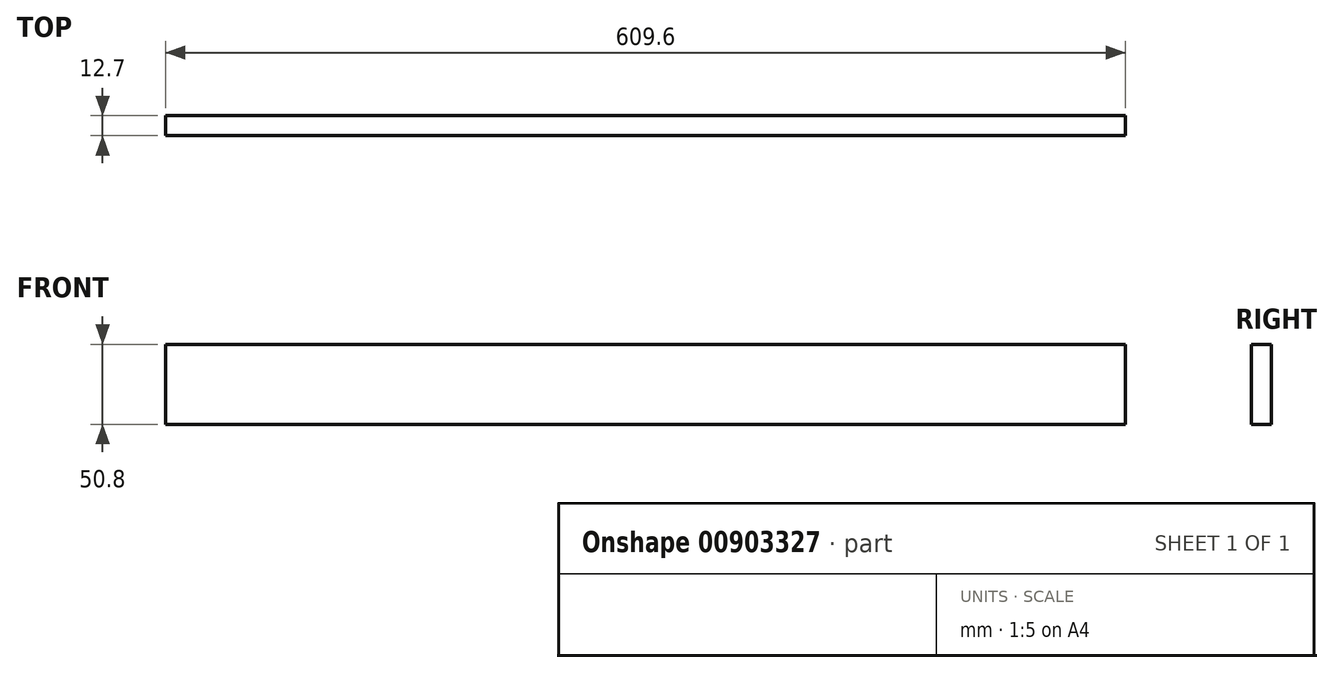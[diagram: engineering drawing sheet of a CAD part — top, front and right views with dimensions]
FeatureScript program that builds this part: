
annotation { "Feature Type Name" : "Feature", "Feature Type Description" : "" }
export const myFeature = defineFeature(function(context is Context, id is Id, definition is map)
    precondition{}
    {
        {
            var Q0;
            Q0=qCreatedBy(makeId("Right.planeOp"),FACE);
            var sketch = newSketch(context, id + "F0", { "sketchPlane" : qUnion([Q0])});
            skLineSegment(sketch, "E0.bottom", {"start": v(-25.21, 17.4) * mm, "end": v(-12.51, 17.4) * mm});
            skLineSegment(sketch, "E0.top", {"start": v(-25.21, -33.4) * mm, "end": v(-12.51, -33.4) * mm});
            skLineSegment(sketch, "E0.left", {"start": v(-25.21, 17.4) * mm, "end": v(-25.21, -33.4) * mm});
            skLineSegment(sketch, "E0.right", {"start": v(-12.51, 17.4) * mm, "end": v(-12.51, -33.4) * mm});
            skSolve(sketch);
        }
        {
            var Q0;
            Q0=makeQuery(id+"F0.imprint","IMPRINT",FACE,{"disambiguationData":[TD([[makeQuery(id+"F0.imprint","IMPRINT",EDGE,{"derivedFrom":sQuery(id+"F0.wireOp",EDGE,"E0.bottom")}),-1.0]])]});
            extrude(context, id + "F1", {"entities" : qUnion([Q0]), "depth" : 609.6 * mm, "offsetDistance" : 25.4 * mm});
        }
    });
